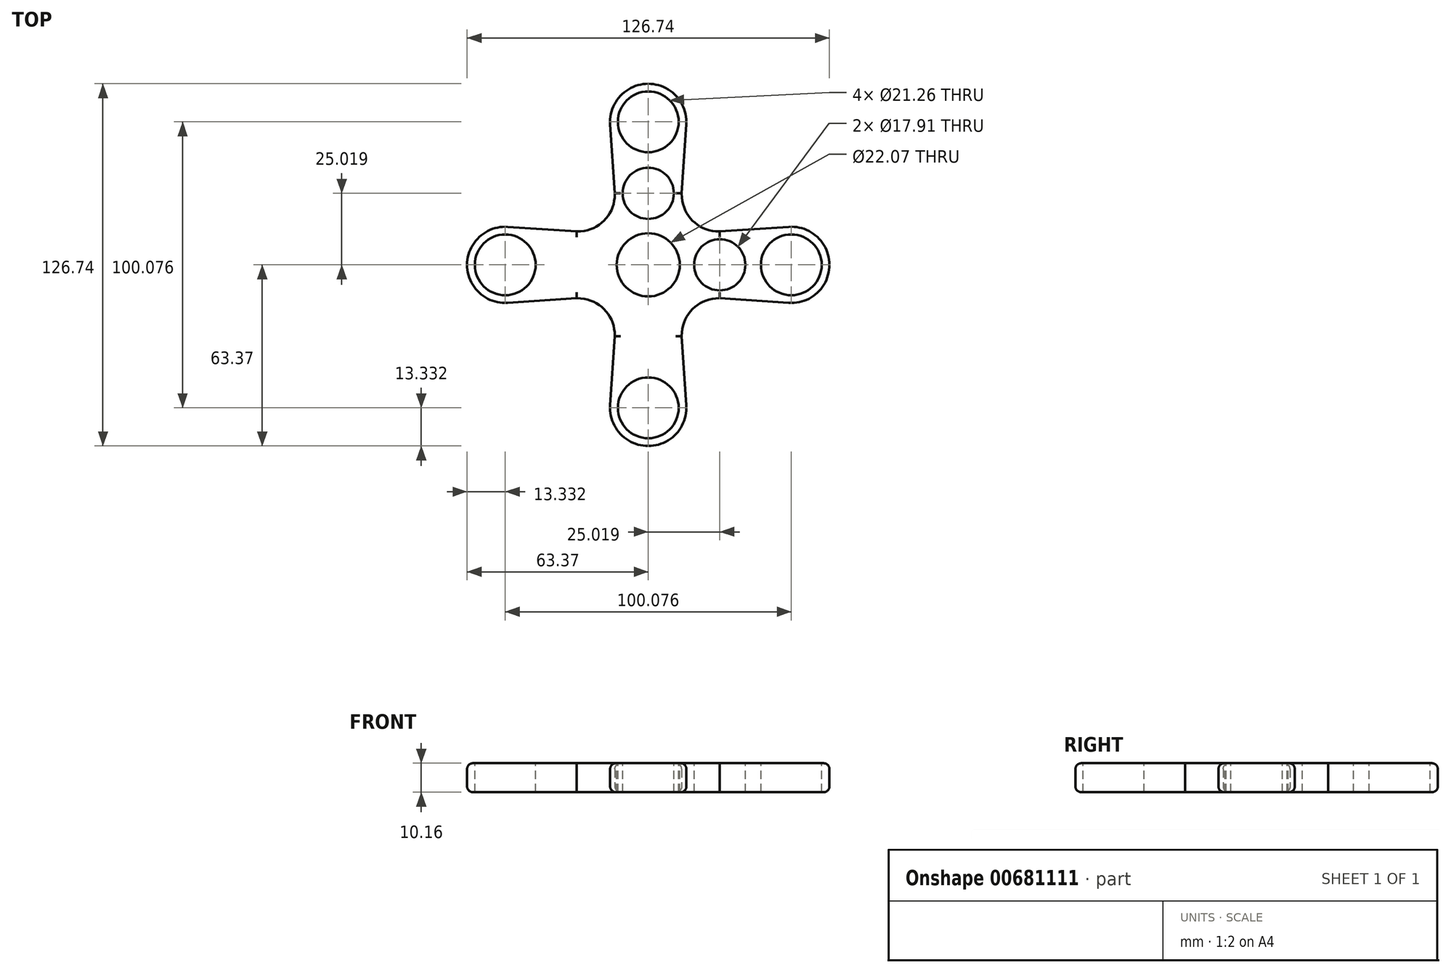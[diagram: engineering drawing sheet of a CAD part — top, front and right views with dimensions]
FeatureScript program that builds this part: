
annotation { "Feature Type Name" : "Feature", "Feature Type Description" : "" }
export const myFeature = defineFeature(function(context is Context, id is Id, definition is map)
    precondition{}
    {
        {
            var Q0;
            Q0=qCreatedBy(makeId("Top.planeOp"),FACE);
            var sketch = newSketch(context, id + "F0", { "sketchPlane" : qUnion([Q0])});
            skCircle(sketch, "E0", {"center": v(0, 0) * mm, "radius": 13.34 * mm});
            skLineSegment(sketch, "E1", {"start": v(0, 0) * mm, "end": v(0, 50.04) * mm});
            skLineSegment(sketch, "E2", {"start": v(0, 0) * mm, "end": v(-50.04, 0) * mm});
            skLineSegment(sketch, "E3", {"start": v(0, 0) * mm, "end": v(50.04, 0) * mm});
            skLineSegment(sketch, "E4", {"start": v(0, 0) * mm, "end": v(0, -50.04) * mm});
            skCircle(sketch, "E5", {"center": v(0, 25.02) * mm, "radius": 11.66 * mm});
            skCircle(sketch, "E6", {"center": v(-25.02, 0) * mm, "radius": 11.66 * mm});
            skCircle(sketch, "E7", {"center": v(25.02, 0) * mm, "radius": 11.66 * mm});
            skCircle(sketch, "E8", {"center": v(0, -25.02) * mm, "radius": 11.66 * mm});
            skCircle(sketch, "E9", {"center": v(0, 50.04) * mm, "radius": 13.34 * mm});
            skCircle(sketch, "E10", {"center": v(-50.04, 0) * mm, "radius": 13.34 * mm});
            skCircle(sketch, "E11", {"center": v(50.04, 0) * mm, "radius": 13.34 * mm});
            skCircle(sketch, "E12", {"center": v(0, -50.04) * mm, "radius": 13.34 * mm});
            skLineSegment(sketch, "E13", {"start": v(-49.14, -13.3) * mm, "end": v(-24.24, -11.63) * mm});
            skLineSegment(sketch, "E14", {"start": v(-49.14, 13.3) * mm, "end": v(-24.24, 11.63) * mm});
            skLineSegment(sketch, "E15", {"start": v(-11.63, -24.24) * mm, "end": v(-13.3, -49.14) * mm});
            skLineSegment(sketch, "E16", {"start": v(11.63, -24.24) * mm, "end": v(13.3, -49.14) * mm});
            skLineSegment(sketch, "E17", {"start": v(24.24, 11.63) * mm, "end": v(49.14, 13.3) * mm});
            skLineSegment(sketch, "E18", {"start": v(24.24, -11.63) * mm, "end": v(49.14, -13.3) * mm});
            skLineSegment(sketch, "E19", {"start": v(-13.3, 49.14) * mm, "end": v(-11.63, 24.24) * mm});
            skLineSegment(sketch, "E20", {"start": v(11.63, 24.24) * mm, "end": v(13.3, 49.14) * mm});
            skLineSegment(sketch, "E21", {"start": v(-25.02, -11.68) * mm, "end": v(-0.9, -13.3) * mm});
            skLineSegment(sketch, "E22", {"start": v(-25.02, 11.68) * mm, "end": v(-0.9, 13.3) * mm});
            skLineSegment(sketch, "E23", {"start": v(-11.68, -25.02) * mm, "end": v(-13.3, -0.9) * mm});
            skLineSegment(sketch, "E24", {"start": v(11.68, -25.02) * mm, "end": v(13.3, -0.9) * mm});
            skLineSegment(sketch, "E25", {"start": v(25.02, -11.68) * mm, "end": v(0.9, -13.3) * mm});
            skLineSegment(sketch, "E26", {"start": v(25.02, 11.68) * mm, "end": v(0.9, 13.3) * mm});
            skLineSegment(sketch, "E27", {"start": v(11.68, 25.02) * mm, "end": v(13.3, 0.9) * mm});
            skLineSegment(sketch, "E28", {"start": v(-11.68, 25.02) * mm, "end": v(-13.3, 0.9) * mm});
            skSolve(sketch);
        }
        {
            var Q0;
            {var subQ0=sQuery(id+"F0.wireOp",EDGE,"E9");var subQ1=makeQuery(id+"F0.imprint","INTERSECT",VERTEX,{"derivedFrom":[subQ0,sQuery(id+"F0.wireOp",EDGE,"E19")]});Q0=makeQuery(id+"F0.imprint","IMPRINT",FACE,{"disambiguationData":[TD([[makeQuery(id+"F0.imprint","IMPRINT",EDGE,{"disambiguationData":[TD([[subQ1,-1.0]])],"derivedFrom":subQ0}),1.0]])]});}
            var Q1;
            {var subQ5=sQuery(id+"F0.wireOp",EDGE,"E9");var subQ7=sQuery(id+"F0.wireOp",EDGE,"E1");var subQ8=makeQuery(id+"F0.imprint","INTERSECT",VERTEX,{"derivedFrom":[subQ7,subQ5]});Q1=makeQuery(id+"F0.imprint","IMPRINT",FACE,{"disambiguationData":[TD([[makeQuery(id+"F0.imprint","IMPRINT",EDGE,{"disambiguationData":[TD([[subQ8,1.0]])],"derivedFrom":subQ7}),1.0]])]});}
            var Q2;
            {var subQ5=sQuery(id+"F0.wireOp",EDGE,"E9");var subQ7=sQuery(id+"F0.wireOp",EDGE,"E1");var subQ8=makeQuery(id+"F0.imprint","INTERSECT",VERTEX,{"derivedFrom":[subQ7,subQ5]});Q2=makeQuery(id+"F0.imprint","IMPRINT",FACE,{"disambiguationData":[TD([[makeQuery(id+"F0.imprint","IMPRINT",EDGE,{"disambiguationData":[TD([[subQ8,1.0]])],"derivedFrom":subQ7}),-1.0]])]});}
            var Q3;
            {var subQ0=sQuery(id+"F0.wireOp",EDGE,"E5");var subQ1=sQuery(id+"F0.wireOp",EDGE,"E1");var subQ2=makeQuery(id+"F0.imprint","INTERSECT",VERTEX,{"disambiguationData":[OD(0.0)],"derivedFrom":[subQ1,subQ0]});Q3=makeQuery(id+"F0.imprint","IMPRINT",FACE,{"disambiguationData":[TD([[makeQuery(id+"F0.imprint","IMPRINT",EDGE,{"disambiguationData":[TD([[subQ2,-1.0]])],"derivedFrom":subQ1}),-1.0]])]});}
            var Q4;
            {var subQ0=sQuery(id+"F0.wireOp",EDGE,"E5");var subQ1=sQuery(id+"F0.wireOp",EDGE,"E1");var subQ2=makeQuery(id+"F0.imprint","INTERSECT",VERTEX,{"disambiguationData":[OD(0.0)],"derivedFrom":[subQ1,subQ0]});Q4=makeQuery(id+"F0.imprint","IMPRINT",FACE,{"disambiguationData":[TD([[makeQuery(id+"F0.imprint","IMPRINT",EDGE,{"disambiguationData":[TD([[subQ2,-1.0]])],"derivedFrom":subQ1}),1.0]])]});}
            var Q5;
            {var subQ0=sQuery(id+"F0.wireOp",EDGE,"E10");var subQ1=makeQuery(id+"F0.imprint","INTERSECT",VERTEX,{"derivedFrom":[subQ0,sQuery(id+"F0.wireOp",EDGE,"E14")]});Q5=makeQuery(id+"F0.imprint","IMPRINT",FACE,{"disambiguationData":[TD([[makeQuery(id+"F0.imprint","IMPRINT",EDGE,{"disambiguationData":[TD([[subQ1,1.0]])],"derivedFrom":subQ0}),1.0]])]});}
            var Q6;
            {var subQ1=sQuery(id+"F0.wireOp",EDGE,"E10");var subQ3=sQuery(id+"F0.wireOp",EDGE,"E2");var subQ4=makeQuery(id+"F0.imprint","INTERSECT",VERTEX,{"derivedFrom":[subQ3,subQ1]});Q6=makeQuery(id+"F0.imprint","IMPRINT",FACE,{"disambiguationData":[TD([[makeQuery(id+"F0.imprint","IMPRINT",EDGE,{"disambiguationData":[TD([[subQ4,1.0]])],"derivedFrom":subQ3}),-1.0]])]});}
            var Q7;
            {var subQ1=sQuery(id+"F0.wireOp",EDGE,"E10");var subQ3=sQuery(id+"F0.wireOp",EDGE,"E2");var subQ4=makeQuery(id+"F0.imprint","INTERSECT",VERTEX,{"derivedFrom":[subQ3,subQ1]});Q7=makeQuery(id+"F0.imprint","IMPRINT",FACE,{"disambiguationData":[TD([[makeQuery(id+"F0.imprint","IMPRINT",EDGE,{"disambiguationData":[TD([[subQ4,1.0]])],"derivedFrom":subQ3}),1.0]])]});}
            var Q8;
            {var subQ0=sQuery(id+"F0.wireOp",EDGE,"E6");var subQ1=sQuery(id+"F0.wireOp",EDGE,"E2");var subQ2=makeQuery(id+"F0.imprint","INTERSECT",VERTEX,{"disambiguationData":[OD(0.0)],"derivedFrom":[subQ1,subQ0]});Q8=makeQuery(id+"F0.imprint","IMPRINT",FACE,{"disambiguationData":[TD([[makeQuery(id+"F0.imprint","IMPRINT",EDGE,{"disambiguationData":[TD([[subQ2,-1.0]])],"derivedFrom":subQ1}),-1.0]])]});}
            var Q9;
            {var subQ0=sQuery(id+"F0.wireOp",EDGE,"E6");var subQ1=sQuery(id+"F0.wireOp",EDGE,"E2");var subQ2=makeQuery(id+"F0.imprint","INTERSECT",VERTEX,{"disambiguationData":[OD(0.0)],"derivedFrom":[subQ1,subQ0]});Q9=makeQuery(id+"F0.imprint","IMPRINT",FACE,{"disambiguationData":[TD([[makeQuery(id+"F0.imprint","IMPRINT",EDGE,{"disambiguationData":[TD([[subQ2,-1.0]])],"derivedFrom":subQ1}),1.0]])]});}
            var Q10;
            {var subQ0=sQuery(id+"F0.wireOp",EDGE,"E12");var subQ1=makeQuery(id+"F0.imprint","INTERSECT",VERTEX,{"derivedFrom":[subQ0,sQuery(id+"F0.wireOp",EDGE,"E16")]});Q10=makeQuery(id+"F0.imprint","IMPRINT",FACE,{"disambiguationData":[TD([[makeQuery(id+"F0.imprint","IMPRINT",EDGE,{"disambiguationData":[TD([[subQ1,-1.0]])],"derivedFrom":subQ0}),1.0]])]});}
            var Q11;
            {var subQ5=sQuery(id+"F0.wireOp",EDGE,"E12");var subQ7=sQuery(id+"F0.wireOp",EDGE,"E4");var subQ8=makeQuery(id+"F0.imprint","INTERSECT",VERTEX,{"derivedFrom":[subQ7,subQ5]});Q11=makeQuery(id+"F0.imprint","IMPRINT",FACE,{"disambiguationData":[TD([[makeQuery(id+"F0.imprint","IMPRINT",EDGE,{"disambiguationData":[TD([[subQ8,1.0]])],"derivedFrom":subQ7}),1.0]])]});}
            var Q12;
            {var subQ5=sQuery(id+"F0.wireOp",EDGE,"E4");var subQ7=sQuery(id+"F0.wireOp",EDGE,"E12");var subQ8=makeQuery(id+"F0.imprint","INTERSECT",VERTEX,{"derivedFrom":[subQ5,subQ7]});Q12=makeQuery(id+"F0.imprint","IMPRINT",FACE,{"disambiguationData":[TD([[makeQuery(id+"F0.imprint","IMPRINT",EDGE,{"disambiguationData":[TD([[subQ8,1.0]])],"derivedFrom":subQ5}),-1.0]])]});}
            var Q13;
            {var subQ0=sQuery(id+"F0.wireOp",EDGE,"E8");var subQ1=sQuery(id+"F0.wireOp",EDGE,"E4");var subQ2=makeQuery(id+"F0.imprint","INTERSECT",VERTEX,{"disambiguationData":[OD(0.0)],"derivedFrom":[subQ1,subQ0]});Q13=makeQuery(id+"F0.imprint","IMPRINT",FACE,{"disambiguationData":[TD([[makeQuery(id+"F0.imprint","IMPRINT",EDGE,{"disambiguationData":[TD([[subQ2,-1.0]])],"derivedFrom":subQ1}),-1.0]])]});}
            var Q14;
            {var subQ0=sQuery(id+"F0.wireOp",EDGE,"E8");var subQ1=sQuery(id+"F0.wireOp",EDGE,"E4");var subQ2=makeQuery(id+"F0.imprint","INTERSECT",VERTEX,{"disambiguationData":[OD(0.0)],"derivedFrom":[subQ1,subQ0]});Q14=makeQuery(id+"F0.imprint","IMPRINT",FACE,{"disambiguationData":[TD([[makeQuery(id+"F0.imprint","IMPRINT",EDGE,{"disambiguationData":[TD([[subQ2,-1.0]])],"derivedFrom":subQ1}),1.0]])]});}
            var Q15;
            {var subQ0=sQuery(id+"F0.wireOp",EDGE,"E7");var subQ1=sQuery(id+"F0.wireOp",EDGE,"E3");var subQ2=makeQuery(id+"F0.imprint","INTERSECT",VERTEX,{"disambiguationData":[OD(0.0)],"derivedFrom":[subQ1,subQ0]});Q15=makeQuery(id+"F0.imprint","IMPRINT",FACE,{"disambiguationData":[TD([[makeQuery(id+"F0.imprint","IMPRINT",EDGE,{"disambiguationData":[TD([[subQ2,-1.0]])],"derivedFrom":subQ1}),-1.0]])]});}
            var Q16;
            {var subQ0=sQuery(id+"F0.wireOp",EDGE,"E7");var subQ1=sQuery(id+"F0.wireOp",EDGE,"E3");var subQ2=makeQuery(id+"F0.imprint","INTERSECT",VERTEX,{"disambiguationData":[OD(0.0)],"derivedFrom":[subQ1,subQ0]});Q16=makeQuery(id+"F0.imprint","IMPRINT",FACE,{"disambiguationData":[TD([[makeQuery(id+"F0.imprint","IMPRINT",EDGE,{"disambiguationData":[TD([[subQ2,-1.0]])],"derivedFrom":subQ1}),1.0]])]});}
            var Q17;
            {var subQ5=sQuery(id+"F0.wireOp",EDGE,"E11");var subQ6=sQuery(id+"F0.wireOp",EDGE,"E3");var subQ7=makeQuery(id+"F0.imprint","INTERSECT",VERTEX,{"derivedFrom":[subQ6,subQ5]});Q17=makeQuery(id+"F0.imprint","IMPRINT",FACE,{"disambiguationData":[TD([[makeQuery(id+"F0.imprint","IMPRINT",EDGE,{"disambiguationData":[TD([[subQ7,1.0]])],"derivedFrom":subQ6}),1.0]])]});}
            var Q18;
            {var subQ5=sQuery(id+"F0.wireOp",EDGE,"E11");var subQ7=sQuery(id+"F0.wireOp",EDGE,"E3");var subQ8=makeQuery(id+"F0.imprint","INTERSECT",VERTEX,{"derivedFrom":[subQ7,subQ5]});Q18=makeQuery(id+"F0.imprint","IMPRINT",FACE,{"disambiguationData":[TD([[makeQuery(id+"F0.imprint","IMPRINT",EDGE,{"disambiguationData":[TD([[subQ8,1.0]])],"derivedFrom":subQ7}),-1.0]])]});}
            var Q19;
            {var subQ0=sQuery(id+"F0.wireOp",EDGE,"E11");var subQ1=makeQuery(id+"F0.imprint","INTERSECT",VERTEX,{"derivedFrom":[subQ0,sQuery(id+"F0.wireOp",EDGE,"E17")]});Q19=makeQuery(id+"F0.imprint","IMPRINT",FACE,{"disambiguationData":[TD([[makeQuery(id+"F0.imprint","IMPRINT",EDGE,{"disambiguationData":[TD([[subQ1,-1.0]])],"derivedFrom":subQ0}),1.0]])]});}
            var Q20;
            {var subQ0=sQuery(id+"F0.wireOp",EDGE,"E0");var subQ6=makeQuery(id+"F0.imprint","INTERSECT",VERTEX,{"derivedFrom":[subQ0,sQuery(id+"F0.wireOp",EDGE,"OeqATU7r-TeiP-DVcz-Oj9g-SgelYqET2oCf")]});Q20=makeQuery(id+"F0.imprint","IMPRINT",FACE,{"disambiguationData":[TD([[makeQuery(id+"F0.imprint","IMPRINT",EDGE,{"disambiguationData":[TD([[subQ6,1.0]])],"derivedFrom":subQ0}),1.0]])]});}
            var Q21;
            {var subQ3=sQuery(id+"F0.wireOp",EDGE,"E0");var subQ6=makeQuery(id+"F0.imprint","INTERSECT",VERTEX,{"derivedFrom":[subQ3,sQuery(id+"F0.wireOp",EDGE,"P4mx4NLA-dkh0-m4Ix-icL6-COEjfOKkm9sa")]});Q21=makeQuery(id+"F0.imprint","IMPRINT",FACE,{"disambiguationData":[TD([[makeQuery(id+"F0.imprint","IMPRINT",EDGE,{"disambiguationData":[TD([[subQ6,1.0]])],"derivedFrom":subQ3}),1.0]])]});}
            var Q22;
            {var subQ3=sQuery(id+"F0.wireOp",EDGE,"E0");var subQ7=makeQuery(id+"F0.imprint","INTERSECT",VERTEX,{"derivedFrom":[subQ3,sQuery(id+"F0.wireOp",EDGE,"11MBrxAj-xtIt-JD5e-sfVu-Mb8FnMuhDSvx")]});Q22=makeQuery(id+"F0.imprint","IMPRINT",FACE,{"disambiguationData":[TD([[makeQuery(id+"F0.imprint","IMPRINT",EDGE,{"disambiguationData":[TD([[subQ7,1.0]])],"derivedFrom":subQ3}),1.0]])]});}
            var Q23;
            {var subQ0=sQuery(id+"F0.wireOp",EDGE,"E0");var subQ4=makeQuery(id+"F0.imprint","INTERSECT",VERTEX,{"derivedFrom":[subQ0,sQuery(id+"F0.wireOp",EDGE,"6knshsRv-X30w-t9dV-kw8X-9zXHXomt9KH4")]});Q23=makeQuery(id+"F0.imprint","IMPRINT",FACE,{"disambiguationData":[TD([[makeQuery(id+"F0.imprint","IMPRINT",EDGE,{"disambiguationData":[TD([[subQ4,1.0]])],"derivedFrom":subQ0}),1.0]])]});}
            var Q24;
            {var subQ0=sQuery(id+"F0.wireOp",EDGE,"6knshsRv-X30w-t9dV-kw8X-9zXHXomt9KH4");var subQ1=sQuery(id+"F0.wireOp",EDGE,"E0");var subQ2=makeQuery(id+"F0.imprint","INTERSECT",VERTEX,{"derivedFrom":[subQ1,subQ0]});Q24=makeQuery(id+"F0.imprint","IMPRINT",FACE,{"disambiguationData":[TD([[makeQuery(id+"F0.imprint","IMPRINT",EDGE,{"disambiguationData":[TD([[subQ2,-1.0]])],"derivedFrom":subQ1}),-1.0]])]});}
            var Q25;
            {var subQ0=sQuery(id+"F0.wireOp",EDGE,"xMuVBNXP-0rYr-ahyC-m8RB-kHPSgdyuj2Vt");var subQ1=sQuery(id+"F0.wireOp",EDGE,"E0");var subQ2=makeQuery(id+"F0.imprint","INTERSECT",VERTEX,{"derivedFrom":[subQ1,subQ0]});Q25=makeQuery(id+"F0.imprint","IMPRINT",FACE,{"disambiguationData":[TD([[makeQuery(id+"F0.imprint","IMPRINT",EDGE,{"disambiguationData":[TD([[subQ2,1.0]])],"derivedFrom":subQ1}),-1.0]])]});}
            var Q26;
            {var subQ0=sQuery(id+"F0.wireOp",EDGE,"11MBrxAj-xtIt-JD5e-sfVu-Mb8FnMuhDSvx");var subQ1=sQuery(id+"F0.wireOp",EDGE,"E0");var subQ2=makeQuery(id+"F0.imprint","INTERSECT",VERTEX,{"derivedFrom":[subQ1,subQ0]});Q26=makeQuery(id+"F0.imprint","IMPRINT",FACE,{"disambiguationData":[TD([[makeQuery(id+"F0.imprint","IMPRINT",EDGE,{"disambiguationData":[TD([[subQ2,-1.0]])],"derivedFrom":subQ1}),-1.0]])]});}
            var Q27;
            {var subQ0=sQuery(id+"F0.wireOp",EDGE,"dGcYwOTv-s8BC-CkCZ-X2qb-BfbS53vJcPqF");var subQ1=sQuery(id+"F0.wireOp",EDGE,"E0");var subQ2=makeQuery(id+"F0.imprint","INTERSECT",VERTEX,{"derivedFrom":[subQ1,subQ0]});Q27=makeQuery(id+"F0.imprint","IMPRINT",FACE,{"disambiguationData":[TD([[makeQuery(id+"F0.imprint","IMPRINT",EDGE,{"disambiguationData":[TD([[subQ2,1.0]])],"derivedFrom":subQ1}),-1.0]])]});}
            var Q28;
            {var subQ5=sQuery(id+"F0.wireOp",EDGE,"E0");var subQ9=sQuery(id+"F0.wireOp",EDGE,"0KCwkMXI-Bwza-oeRS-AiLC-Ybub9KsOqaBf");var subQ11=makeQuery(id+"F0.imprint","INTERSECT",VERTEX,{"derivedFrom":[subQ5,subQ9]});Q28=makeQuery(id+"F0.imprint","IMPRINT",FACE,{"disambiguationData":[TD([[makeQuery(id+"F0.imprint","IMPRINT",EDGE,{"disambiguationData":[TD([[subQ11,-1.0]])],"derivedFrom":subQ5}),-1.0]])]});}
            var Q29;
            {var subQ5=sQuery(id+"F0.wireOp",EDGE,"6knshsRv-X30w-t9dV-kw8X-9zXHXomt9KH4");var subQ9=sQuery(id+"F0.wireOp",EDGE,"E0");var subQ11=makeQuery(id+"F0.imprint","INTERSECT",VERTEX,{"derivedFrom":[subQ9,subQ5]});Q29=makeQuery(id+"F0.imprint","IMPRINT",FACE,{"disambiguationData":[TD([[makeQuery(id+"F0.imprint","IMPRINT",EDGE,{"disambiguationData":[TD([[subQ11,1.0]])],"derivedFrom":subQ9}),-1.0]])]});}
            var Q30;
            {var subQ7=sQuery(id+"F0.wireOp",EDGE,"E28");var subQ8=sQuery(id+"F0.wireOp",EDGE,"E0");var subQ9=makeQuery(id+"F0.imprint","INTERSECT",VERTEX,{"derivedFrom":[subQ8,subQ7]});Q30=makeQuery(id+"F0.imprint","IMPRINT",FACE,{"disambiguationData":[TD([[makeQuery(id+"F0.imprint","IMPRINT",EDGE,{"disambiguationData":[TD([[subQ9,-1.0]])],"derivedFrom":subQ8}),-1.0]])]});}
            var Q31;
            {var subQ7=sQuery(id+"F0.wireOp",EDGE,"E0");var subQ9=sQuery(id+"F0.wireOp",EDGE,"E23");var subQ10=makeQuery(id+"F0.imprint","INTERSECT",VERTEX,{"derivedFrom":[subQ7,subQ9]});Q31=makeQuery(id+"F0.imprint","IMPRINT",FACE,{"disambiguationData":[TD([[makeQuery(id+"F0.imprint","IMPRINT",EDGE,{"disambiguationData":[TD([[subQ10,1.0]])],"derivedFrom":subQ7}),-1.0]])]});}
            var Q32;
            {var subQ5=sQuery(id+"F0.wireOp",EDGE,"E22");var subQ6=sQuery(id+"F0.wireOp",EDGE,"E0");var subQ7=makeQuery(id+"F0.imprint","INTERSECT",VERTEX,{"derivedFrom":[subQ6,subQ5]});Q32=makeQuery(id+"F0.imprint","IMPRINT",FACE,{"disambiguationData":[TD([[makeQuery(id+"F0.imprint","IMPRINT",EDGE,{"disambiguationData":[TD([[subQ7,1.0]])],"derivedFrom":subQ6}),-1.0]])]});}
            var Q33;
            {var subQ7=sQuery(id+"F0.wireOp",EDGE,"E0");var subQ9=sQuery(id+"F0.wireOp",EDGE,"E26");var subQ10=makeQuery(id+"F0.imprint","INTERSECT",VERTEX,{"derivedFrom":[subQ7,subQ9]});Q33=makeQuery(id+"F0.imprint","IMPRINT",FACE,{"disambiguationData":[TD([[makeQuery(id+"F0.imprint","IMPRINT",EDGE,{"disambiguationData":[TD([[subQ10,-1.0]])],"derivedFrom":subQ7}),-1.0]])]});}
            var Q34;
            {var subQ7=sQuery(id+"F0.wireOp",EDGE,"E0");var subQ9=sQuery(id+"F0.wireOp",EDGE,"E27");var subQ10=makeQuery(id+"F0.imprint","INTERSECT",VERTEX,{"derivedFrom":[subQ7,subQ9]});Q34=makeQuery(id+"F0.imprint","IMPRINT",FACE,{"disambiguationData":[TD([[makeQuery(id+"F0.imprint","IMPRINT",EDGE,{"disambiguationData":[TD([[subQ10,1.0]])],"derivedFrom":subQ7}),-1.0]])]});}
            var Q35;
            {var subQ7=sQuery(id+"F0.wireOp",EDGE,"E24");var subQ8=sQuery(id+"F0.wireOp",EDGE,"E0");var subQ9=makeQuery(id+"F0.imprint","INTERSECT",VERTEX,{"derivedFrom":[subQ8,subQ7]});Q35=makeQuery(id+"F0.imprint","IMPRINT",FACE,{"disambiguationData":[TD([[makeQuery(id+"F0.imprint","IMPRINT",EDGE,{"disambiguationData":[TD([[subQ9,-1.0]])],"derivedFrom":subQ8}),-1.0]])]});}
            var Q36;
            {var subQ7=sQuery(id+"F0.wireOp",EDGE,"E0");var subQ9=sQuery(id+"F0.wireOp",EDGE,"E25");var subQ10=makeQuery(id+"F0.imprint","INTERSECT",VERTEX,{"derivedFrom":[subQ7,subQ9]});Q36=makeQuery(id+"F0.imprint","IMPRINT",FACE,{"disambiguationData":[TD([[makeQuery(id+"F0.imprint","IMPRINT",EDGE,{"disambiguationData":[TD([[subQ10,1.0]])],"derivedFrom":subQ7}),-1.0]])]});}
            var Q37;
            {var subQ5=sQuery(id+"F0.wireOp",EDGE,"E21");var subQ6=sQuery(id+"F0.wireOp",EDGE,"E0");var subQ7=makeQuery(id+"F0.imprint","INTERSECT",VERTEX,{"derivedFrom":[subQ6,subQ5]});Q37=makeQuery(id+"F0.imprint","IMPRINT",FACE,{"disambiguationData":[TD([[makeQuery(id+"F0.imprint","IMPRINT",EDGE,{"disambiguationData":[TD([[subQ7,-1.0]])],"derivedFrom":subQ6}),-1.0]])]});}
            extrude(context, id + "F1", {"entities" : qUnion([Q0, Q1, Q2, Q3, Q4, Q5, Q6, Q7, Q8, Q9, Q10, Q11, Q12, Q13, Q14, Q15, Q16, Q17, Q18, Q19, Q20, Q21, Q22, Q23, Q24, Q25, Q26, Q27, Q28, Q29, Q30, Q31, Q32, Q33, Q34, Q35, Q36, Q37]), "depth" : 10.16 * mm, "offsetDistance" : 25.4 * mm});
        }
        {
            var Q0;
            Q0=makeQuery(id+"F1.opExtrude","CAP_FACE",FACE,{"disambiguationData":[OSD([sQuery(id+"F0.wireOp",EDGE,"E9"),sQuery(id+"F0.wireOp",EDGE,"E10"),sQuery(id+"F0.wireOp",EDGE,"E11"),sQuery(id+"F0.wireOp",EDGE,"E12"),sQuery(id+"F0.wireOp",EDGE,"E13"),sQuery(id+"F0.wireOp",EDGE,"E14"),sQuery(id+"F0.wireOp",EDGE,"E15"),sQuery(id+"F0.wireOp",EDGE,"E16"),sQuery(id+"F0.wireOp",EDGE,"E17"),sQuery(id+"F0.wireOp",EDGE,"E18"),sQuery(id+"F0.wireOp",EDGE,"E19"),sQuery(id+"F0.wireOp",EDGE,"E20"),sQuery(id+"F0.wireOp",EDGE,"E21"),sQuery(id+"F0.wireOp",EDGE,"E22"),sQuery(id+"F0.wireOp",EDGE,"E23"),sQuery(id+"F0.wireOp",EDGE,"E24"),sQuery(id+"F0.wireOp",EDGE,"E25"),sQuery(id+"F0.wireOp",EDGE,"E26"),sQuery(id+"F0.wireOp",EDGE,"E27"),sQuery(id+"F0.wireOp",EDGE,"E28")])],"isStart":false});
            var sketch = newSketch(context, id + "F2", { "sketchPlane" : qUnion([Q0])});
            skCircle(sketch, "E29", {"center": v(0, 50.04) * mm, "radius": 10.63 * mm});
            skCircle(sketch, "E30", {"center": v(-50.04, 0) * mm, "radius": 10.63 * mm});
            skCircle(sketch, "E31", {"center": v(50.04, 0) * mm, "radius": 10.63 * mm});
            skCircle(sketch, "E32", {"center": v(0, -50.04) * mm, "radius": 10.63 * mm});
            skCircle(sketch, "E33", {"center": v(0, 0) * mm, "radius": 11.04 * mm});
            skLineSegment(sketch, "E34", {"start": v(0, 0) * mm, "end": v(-50.04, 0) * mm});
            skLineSegment(sketch, "E35", {"start": v(0, 0) * mm, "end": v(50.04, 0) * mm});
            skLineSegment(sketch, "E36", {"start": v(0, 0) * mm, "end": v(0, 50.04) * mm});
            skLineSegment(sketch, "E37", {"start": v(0, 0) * mm, "end": v(0, -50.04) * mm});
            skCircle(sketch, "E38", {"center": v(-25.02, 0) * mm, "radius": 8.95 * mm});
            skCircle(sketch, "E39", {"center": v(25.02, 0) * mm, "radius": 8.95 * mm});
            skCircle(sketch, "E40", {"center": v(0, 25.02) * mm, "radius": 8.95 * mm});
            skCircle(sketch, "E41", {"center": v(0, -25.02) * mm, "radius": 8.95 * mm});
            skSolve(sketch);
        }
        {
            var Q0;
            Q0=makeQuery(id+"F2.imprint","IMPRINT",FACE,{"disambiguationData":[TD([[makeQuery(id+"F2.imprint","IMPRINT",EDGE,{"derivedFrom":sQuery(id+"F2.wireOp",EDGE,"E29")}),1.0]])]});
            var Q1;
            Q1=makeQuery(id+"F2.imprint","IMPRINT",FACE,{"disambiguationData":[TD([[makeQuery(id+"F2.imprint","IMPRINT",EDGE,{"derivedFrom":sQuery(id+"F2.wireOp",EDGE,"E30")}),1.0]])]});
            var Q2;
            Q2=makeQuery(id+"F2.imprint","IMPRINT",FACE,{"disambiguationData":[TD([[makeQuery(id+"F2.imprint","IMPRINT",EDGE,{"derivedFrom":sQuery(id+"F2.wireOp",EDGE,"E33")}),1.0]])]});
            var Q3;
            Q3=makeQuery(id+"F2.imprint","IMPRINT",FACE,{"disambiguationData":[TD([[makeQuery(id+"F2.imprint","IMPRINT",EDGE,{"derivedFrom":sQuery(id+"F2.wireOp",EDGE,"E31")}),1.0]])]});
            var Q4;
            Q4=makeQuery(id+"F2.imprint","IMPRINT",FACE,{"disambiguationData":[TD([[makeQuery(id+"F2.imprint","IMPRINT",EDGE,{"derivedFrom":sQuery(id+"F2.wireOp",EDGE,"E32")}),1.0]])]});
            var Q5;
            {var subQ0=sQuery(id+"F2.wireOp",EDGE,"P7v9rNYd-zsm6-EBDp-hEL1-8AicFUI8aBt1");var subQ1=sQuery(id+"F2.wireOp",EDGE,"E34");var subQ2=makeQuery(id+"F2.imprint","INTERSECT",VERTEX,{"disambiguationData":[OD(0.0)],"derivedFrom":[subQ1,subQ0]});Q5=makeQuery(id+"F2.imprint","IMPRINT",FACE,{"disambiguationData":[TD([[makeQuery(id+"F2.imprint","IMPRINT",EDGE,{"disambiguationData":[TD([[subQ2,1.0]])],"derivedFrom":subQ1}),-1.0]])]});}
            var Q6;
            {var subQ0=sQuery(id+"F2.wireOp",EDGE,"P7v9rNYd-zsm6-EBDp-hEL1-8AicFUI8aBt1");var subQ1=sQuery(id+"F2.wireOp",EDGE,"E34");var subQ2=makeQuery(id+"F2.imprint","INTERSECT",VERTEX,{"disambiguationData":[OD(0.0)],"derivedFrom":[subQ1,subQ0]});Q6=makeQuery(id+"F2.imprint","IMPRINT",FACE,{"disambiguationData":[TD([[makeQuery(id+"F2.imprint","IMPRINT",EDGE,{"disambiguationData":[TD([[subQ2,1.0]])],"derivedFrom":subQ1}),1.0]])]});}
            var Q7;
            {var subQ0=sQuery(id+"F2.wireOp",EDGE,"sgpK4NKR-6yXJ-TN63-0nZW-uHVtksImcnuz");var subQ1=sQuery(id+"F2.wireOp",EDGE,"E36");var subQ2=makeQuery(id+"F2.imprint","INTERSECT",VERTEX,{"disambiguationData":[OD(0.0)],"derivedFrom":[subQ1,subQ0]});Q7=makeQuery(id+"F2.imprint","IMPRINT",FACE,{"disambiguationData":[TD([[makeQuery(id+"F2.imprint","IMPRINT",EDGE,{"disambiguationData":[TD([[subQ2,-1.0]])],"derivedFrom":subQ1}),1.0]])]});}
            var Q8;
            {var subQ0=sQuery(id+"F2.wireOp",EDGE,"sgpK4NKR-6yXJ-TN63-0nZW-uHVtksImcnuz");var subQ1=sQuery(id+"F2.wireOp",EDGE,"E36");var subQ2=makeQuery(id+"F2.imprint","INTERSECT",VERTEX,{"disambiguationData":[OD(0.0)],"derivedFrom":[subQ1,subQ0]});Q8=makeQuery(id+"F2.imprint","IMPRINT",FACE,{"disambiguationData":[TD([[makeQuery(id+"F2.imprint","IMPRINT",EDGE,{"disambiguationData":[TD([[subQ2,-1.0]])],"derivedFrom":subQ1}),-1.0]])]});}
            var Q9;
            {var subQ0=sQuery(id+"F2.wireOp",EDGE,"QqMhnWJU-l4oD-vyuv-57R4-FaOAJUmgMaoE");var subQ1=sQuery(id+"F2.wireOp",EDGE,"E35");var subQ2=makeQuery(id+"F2.imprint","INTERSECT",VERTEX,{"disambiguationData":[OD(0.0)],"derivedFrom":[subQ1,subQ0]});Q9=makeQuery(id+"F2.imprint","IMPRINT",FACE,{"disambiguationData":[TD([[makeQuery(id+"F2.imprint","IMPRINT",EDGE,{"disambiguationData":[TD([[subQ2,-1.0]])],"derivedFrom":subQ1}),1.0]])]});}
            var Q10;
            {var subQ0=sQuery(id+"F2.wireOp",EDGE,"QqMhnWJU-l4oD-vyuv-57R4-FaOAJUmgMaoE");var subQ1=sQuery(id+"F2.wireOp",EDGE,"E35");var subQ2=makeQuery(id+"F2.imprint","INTERSECT",VERTEX,{"disambiguationData":[OD(0.0)],"derivedFrom":[subQ1,subQ0]});Q10=makeQuery(id+"F2.imprint","IMPRINT",FACE,{"disambiguationData":[TD([[makeQuery(id+"F2.imprint","IMPRINT",EDGE,{"disambiguationData":[TD([[subQ2,-1.0]])],"derivedFrom":subQ1}),-1.0]])]});}
            var Q11;
            {var subQ0=sQuery(id+"F2.wireOp",EDGE,"5nZpbu1R-FvPb-eCDr-ticD-0d8ufeMjPlMW");var subQ1=sQuery(id+"F2.wireOp",EDGE,"E37");var subQ2=makeQuery(id+"F2.imprint","INTERSECT",VERTEX,{"disambiguationData":[OD(0.0)],"derivedFrom":[subQ1,subQ0]});Q11=makeQuery(id+"F2.imprint","IMPRINT",FACE,{"disambiguationData":[TD([[makeQuery(id+"F2.imprint","IMPRINT",EDGE,{"disambiguationData":[TD([[subQ2,1.0]])],"derivedFrom":subQ1}),-1.0]])]});}
            var Q12;
            {var subQ0=sQuery(id+"F2.wireOp",EDGE,"5nZpbu1R-FvPb-eCDr-ticD-0d8ufeMjPlMW");var subQ1=sQuery(id+"F2.wireOp",EDGE,"E37");var subQ2=makeQuery(id+"F2.imprint","INTERSECT",VERTEX,{"disambiguationData":[OD(0.0)],"derivedFrom":[subQ1,subQ0]});Q12=makeQuery(id+"F2.imprint","IMPRINT",FACE,{"disambiguationData":[TD([[makeQuery(id+"F2.imprint","IMPRINT",EDGE,{"disambiguationData":[TD([[subQ2,1.0]])],"derivedFrom":subQ1}),1.0]])]});}
            var Q13;
            {var subQ0=sQuery(id+"F2.wireOp",EDGE,"E38");var subQ1=sQuery(id+"F2.wireOp",EDGE,"E34");var subQ2=makeQuery(id+"F2.imprint","INTERSECT",VERTEX,{"disambiguationData":[OD(0.0)],"derivedFrom":[subQ1,subQ0]});Q13=makeQuery(id+"F2.imprint","IMPRINT",FACE,{"disambiguationData":[TD([[makeQuery(id+"F2.imprint","IMPRINT",EDGE,{"disambiguationData":[TD([[subQ2,1.0]])],"derivedFrom":subQ1}),-1.0]])]});}
            var Q14;
            {var subQ0=sQuery(id+"F2.wireOp",EDGE,"E38");var subQ1=sQuery(id+"F2.wireOp",EDGE,"E34");var subQ2=makeQuery(id+"F2.imprint","INTERSECT",VERTEX,{"disambiguationData":[OD(0.0)],"derivedFrom":[subQ1,subQ0]});Q14=makeQuery(id+"F2.imprint","IMPRINT",FACE,{"disambiguationData":[TD([[makeQuery(id+"F2.imprint","IMPRINT",EDGE,{"disambiguationData":[TD([[subQ2,1.0]])],"derivedFrom":subQ1}),1.0]])]});}
            var Q15;
            {var subQ0=sQuery(id+"F2.wireOp",EDGE,"E40");var subQ1=sQuery(id+"F2.wireOp",EDGE,"E36");var subQ2=makeQuery(id+"F2.imprint","INTERSECT",VERTEX,{"disambiguationData":[OD(0.0)],"derivedFrom":[subQ1,subQ0]});Q15=makeQuery(id+"F2.imprint","IMPRINT",FACE,{"disambiguationData":[TD([[makeQuery(id+"F2.imprint","IMPRINT",EDGE,{"disambiguationData":[TD([[subQ2,-1.0]])],"derivedFrom":subQ1}),1.0]])]});}
            var Q16;
            {var subQ0=sQuery(id+"F2.wireOp",EDGE,"E40");var subQ1=sQuery(id+"F2.wireOp",EDGE,"E36");var subQ2=makeQuery(id+"F2.imprint","INTERSECT",VERTEX,{"disambiguationData":[OD(0.0)],"derivedFrom":[subQ1,subQ0]});Q16=makeQuery(id+"F2.imprint","IMPRINT",FACE,{"disambiguationData":[TD([[makeQuery(id+"F2.imprint","IMPRINT",EDGE,{"disambiguationData":[TD([[subQ2,-1.0]])],"derivedFrom":subQ1}),-1.0]])]});}
            var Q17;
            {var subQ0=sQuery(id+"F2.wireOp",EDGE,"E39");var subQ1=sQuery(id+"F2.wireOp",EDGE,"E35");var subQ2=makeQuery(id+"F2.imprint","INTERSECT",VERTEX,{"disambiguationData":[OD(0.0)],"derivedFrom":[subQ1,subQ0]});Q17=makeQuery(id+"F2.imprint","IMPRINT",FACE,{"disambiguationData":[TD([[makeQuery(id+"F2.imprint","IMPRINT",EDGE,{"disambiguationData":[TD([[subQ2,-1.0]])],"derivedFrom":subQ1}),1.0]])]});}
            var Q18;
            {var subQ0=sQuery(id+"F2.wireOp",EDGE,"E39");var subQ1=sQuery(id+"F2.wireOp",EDGE,"E35");var subQ2=makeQuery(id+"F2.imprint","INTERSECT",VERTEX,{"disambiguationData":[OD(0.0)],"derivedFrom":[subQ1,subQ0]});Q18=makeQuery(id+"F2.imprint","IMPRINT",FACE,{"disambiguationData":[TD([[makeQuery(id+"F2.imprint","IMPRINT",EDGE,{"disambiguationData":[TD([[subQ2,-1.0]])],"derivedFrom":subQ1}),-1.0]])]});}
            var Q19;
            {var subQ0=sQuery(id+"F2.wireOp",EDGE,"E41");var subQ1=sQuery(id+"F2.wireOp",EDGE,"E37");var subQ2=makeQuery(id+"F2.imprint","INTERSECT",VERTEX,{"disambiguationData":[OD(0.0)],"derivedFrom":[subQ1,subQ0]});Q19=makeQuery(id+"F2.imprint","IMPRINT",FACE,{"disambiguationData":[TD([[makeQuery(id+"F2.imprint","IMPRINT",EDGE,{"disambiguationData":[TD([[subQ2,1.0]])],"derivedFrom":subQ1}),1.0]])]});}
            var Q20;
            {var subQ0=sQuery(id+"F2.wireOp",EDGE,"E41");var subQ1=sQuery(id+"F2.wireOp",EDGE,"E37");var subQ2=makeQuery(id+"F2.imprint","INTERSECT",VERTEX,{"disambiguationData":[OD(0.0)],"derivedFrom":[subQ1,subQ0]});Q20=makeQuery(id+"F2.imprint","IMPRINT",FACE,{"disambiguationData":[TD([[makeQuery(id+"F2.imprint","IMPRINT",EDGE,{"disambiguationData":[TD([[subQ2,1.0]])],"derivedFrom":subQ1}),-1.0]])]});}
            var Q21;
            Q21=makeQuery(id+"F1.opExtrude","CAP_FACE",FACE,{"disambiguationData":[OSD([sQuery(id+"F0.wireOp",EDGE,"E9"),sQuery(id+"F0.wireOp",EDGE,"E10"),sQuery(id+"F0.wireOp",EDGE,"E11"),sQuery(id+"F0.wireOp",EDGE,"E12"),sQuery(id+"F0.wireOp",EDGE,"E13"),sQuery(id+"F0.wireOp",EDGE,"E14"),sQuery(id+"F0.wireOp",EDGE,"E15"),sQuery(id+"F0.wireOp",EDGE,"E16"),sQuery(id+"F0.wireOp",EDGE,"E17"),sQuery(id+"F0.wireOp",EDGE,"E18"),sQuery(id+"F0.wireOp",EDGE,"E19"),sQuery(id+"F0.wireOp",EDGE,"E20"),sQuery(id+"F0.wireOp",EDGE,"E21"),sQuery(id+"F0.wireOp",EDGE,"E22"),sQuery(id+"F0.wireOp",EDGE,"E23"),sQuery(id+"F0.wireOp",EDGE,"E24"),sQuery(id+"F0.wireOp",EDGE,"E25"),sQuery(id+"F0.wireOp",EDGE,"E26"),sQuery(id+"F0.wireOp",EDGE,"E27"),sQuery(id+"F0.wireOp",EDGE,"E28")])],"isStart":true});
            extrude(context, id + "F3", {"entities" : qUnion([Q0, Q1, Q2, Q3, Q4, Q5, Q6, Q7, Q8, Q9, Q10, Q11, Q12, Q13, Q14, Q15, Q16, Q17, Q18, Q19, Q20]), "operationType" : NewBodyOperationType.REMOVE, "endBound" : BoundingType.UP_TO_SURFACE, "oppositeDirection" : true, "depth" : 25.4 * mm, "endBoundEntityFace" : qUnion([Q21]), "offsetDistance" : 25.4 * mm});
        }
        {
            var Q0;
            Q0=makeQuery(id+"F1.opExtrude","SWEPT_EDGE",EDGE,{"disambiguationData":[OSD([sQuery(id+"F0.wireOp",EDGE,"E22"),sQuery(id+"F0.wireOp",EDGE,"E28")])]});
            var Q1;
            Q1=makeQuery(id+"F1.opExtrude","SWEPT_EDGE",EDGE,{"disambiguationData":[OSD([sQuery(id+"F0.wireOp",EDGE,"E26"),sQuery(id+"F0.wireOp",EDGE,"E27")])]});
            var Q2;
            Q2=makeQuery(id+"F1.opExtrude","SWEPT_EDGE",EDGE,{"disambiguationData":[OSD([sQuery(id+"F0.wireOp",EDGE,"E24"),sQuery(id+"F0.wireOp",EDGE,"E25")])]});
            var Q3;
            Q3=makeQuery(id+"F1.opExtrude","SWEPT_EDGE",EDGE,{"disambiguationData":[OSD([sQuery(id+"F0.wireOp",EDGE,"E21"),sQuery(id+"F0.wireOp",EDGE,"E23")])]});
            fillet(context, id + "F4", {"entities" : qUnion([Q0, Q1, Q2, Q3]), "radius" : 12.7 * mm, "tangentPropagation" : true, "allowEdgeOverflow" : false});
        }
        {
            var Q0;
            Q0=makeQuery(id+"F1.opExtrude","CAP_EDGE",EDGE,{"disambiguationData":[OSD([sQuery(id+"F0.wireOp",EDGE,"E13")])],"isStart":false});
            var Q1;
            Q1=makeQuery(id+"F1.opExtrude","CAP_EDGE",EDGE,{"disambiguationData":[OSD([sQuery(id+"F0.wireOp",EDGE,"E21")])],"isStart":false});
            var Q2;
            Q2=makeQuery(id+"F1.opExtrude","CAP_EDGE",EDGE,{"disambiguationData":[OSD([sQuery(id+"F0.wireOp",EDGE,"E15")])],"isStart":false});
            var Q3;
            {var subQ0=sQuery(id+"F0.wireOp",EDGE,"E25");var subQ1=sQuery(id+"F0.wireOp",EDGE,"E24");Q3=makeQuery(id+"F4.opFillet","BLEND_EDGE",EDGE,{"blendedFrom":[makeQuery(id+"F1.opExtrude","SWEPT_EDGE",EDGE,{"disambiguationData":[OSD([subQ1,subQ0])]}),makeQuery(id+"F1.opExtrude","CAP_FACE",FACE,{"disambiguationData":[OSD([sQuery(id+"F0.wireOp",EDGE,"E9"),sQuery(id+"F0.wireOp",EDGE,"E10"),sQuery(id+"F0.wireOp",EDGE,"E11"),sQuery(id+"F0.wireOp",EDGE,"E12"),sQuery(id+"F0.wireOp",EDGE,"E13"),sQuery(id+"F0.wireOp",EDGE,"E14"),sQuery(id+"F0.wireOp",EDGE,"E15"),sQuery(id+"F0.wireOp",EDGE,"E16"),sQuery(id+"F0.wireOp",EDGE,"E17"),sQuery(id+"F0.wireOp",EDGE,"E18"),sQuery(id+"F0.wireOp",EDGE,"E19"),sQuery(id+"F0.wireOp",EDGE,"E20"),sQuery(id+"F0.wireOp",EDGE,"E21"),sQuery(id+"F0.wireOp",EDGE,"E22"),sQuery(id+"F0.wireOp",EDGE,"E23"),subQ1,subQ0,sQuery(id+"F0.wireOp",EDGE,"E26"),sQuery(id+"F0.wireOp",EDGE,"E27"),sQuery(id+"F0.wireOp",EDGE,"E28")])],"isStart":false})],"blendedInto":[makeQuery(id+"F1.opExtrude","CAP_FACE",FACE,{"disambiguationData":[OSD([sQuery(id+"F0.wireOp",EDGE,"E9"),sQuery(id+"F0.wireOp",EDGE,"E10"),sQuery(id+"F0.wireOp",EDGE,"E11"),sQuery(id+"F0.wireOp",EDGE,"E12"),sQuery(id+"F0.wireOp",EDGE,"E13"),sQuery(id+"F0.wireOp",EDGE,"E14"),sQuery(id+"F0.wireOp",EDGE,"E15"),sQuery(id+"F0.wireOp",EDGE,"E16"),sQuery(id+"F0.wireOp",EDGE,"E17"),sQuery(id+"F0.wireOp",EDGE,"E18"),sQuery(id+"F0.wireOp",EDGE,"E19"),sQuery(id+"F0.wireOp",EDGE,"E20"),sQuery(id+"F0.wireOp",EDGE,"E21"),sQuery(id+"F0.wireOp",EDGE,"E22"),sQuery(id+"F0.wireOp",EDGE,"E23"),subQ1,subQ0,sQuery(id+"F0.wireOp",EDGE,"E26"),sQuery(id+"F0.wireOp",EDGE,"E27"),sQuery(id+"F0.wireOp",EDGE,"E28")])],"isStart":false})]});}
            var Q4;
            Q4=makeQuery(id+"F1.opExtrude","CAP_EDGE",EDGE,{"disambiguationData":[OSD([sQuery(id+"F0.wireOp",EDGE,"E18")])],"isStart":false});
            var Q5;
            {var subQ0=sQuery(id+"F0.wireOp",EDGE,"E27");var subQ1=sQuery(id+"F0.wireOp",EDGE,"E26");Q5=makeQuery(id+"F4.opFillet","BLEND_EDGE",EDGE,{"blendedFrom":[makeQuery(id+"F1.opExtrude","SWEPT_EDGE",EDGE,{"disambiguationData":[OSD([subQ1,subQ0])]}),makeQuery(id+"F1.opExtrude","CAP_FACE",FACE,{"disambiguationData":[OSD([sQuery(id+"F0.wireOp",EDGE,"E9"),sQuery(id+"F0.wireOp",EDGE,"E10"),sQuery(id+"F0.wireOp",EDGE,"E11"),sQuery(id+"F0.wireOp",EDGE,"E12"),sQuery(id+"F0.wireOp",EDGE,"E13"),sQuery(id+"F0.wireOp",EDGE,"E14"),sQuery(id+"F0.wireOp",EDGE,"E15"),sQuery(id+"F0.wireOp",EDGE,"E16"),sQuery(id+"F0.wireOp",EDGE,"E17"),sQuery(id+"F0.wireOp",EDGE,"E18"),sQuery(id+"F0.wireOp",EDGE,"E19"),sQuery(id+"F0.wireOp",EDGE,"E20"),sQuery(id+"F0.wireOp",EDGE,"E21"),sQuery(id+"F0.wireOp",EDGE,"E22"),sQuery(id+"F0.wireOp",EDGE,"E23"),sQuery(id+"F0.wireOp",EDGE,"E24"),sQuery(id+"F0.wireOp",EDGE,"E25"),subQ1,subQ0,sQuery(id+"F0.wireOp",EDGE,"E28")])],"isStart":false})],"blendedInto":[makeQuery(id+"F1.opExtrude","CAP_FACE",FACE,{"disambiguationData":[OSD([sQuery(id+"F0.wireOp",EDGE,"E9"),sQuery(id+"F0.wireOp",EDGE,"E10"),sQuery(id+"F0.wireOp",EDGE,"E11"),sQuery(id+"F0.wireOp",EDGE,"E12"),sQuery(id+"F0.wireOp",EDGE,"E13"),sQuery(id+"F0.wireOp",EDGE,"E14"),sQuery(id+"F0.wireOp",EDGE,"E15"),sQuery(id+"F0.wireOp",EDGE,"E16"),sQuery(id+"F0.wireOp",EDGE,"E17"),sQuery(id+"F0.wireOp",EDGE,"E18"),sQuery(id+"F0.wireOp",EDGE,"E19"),sQuery(id+"F0.wireOp",EDGE,"E20"),sQuery(id+"F0.wireOp",EDGE,"E21"),sQuery(id+"F0.wireOp",EDGE,"E22"),sQuery(id+"F0.wireOp",EDGE,"E23"),sQuery(id+"F0.wireOp",EDGE,"E24"),sQuery(id+"F0.wireOp",EDGE,"E25"),subQ1,subQ0,sQuery(id+"F0.wireOp",EDGE,"E28")])],"isStart":false})]});}
            var Q6;
            Q6=makeQuery(id+"F1.opExtrude","CAP_EDGE",EDGE,{"disambiguationData":[OSD([sQuery(id+"F0.wireOp",EDGE,"E20")])],"isStart":false});
            var Q7;
            {var subQ0=sQuery(id+"F0.wireOp",EDGE,"E28");var subQ1=sQuery(id+"F0.wireOp",EDGE,"E22");Q7=makeQuery(id+"F4.opFillet","BLEND_EDGE",EDGE,{"blendedFrom":[makeQuery(id+"F1.opExtrude","SWEPT_EDGE",EDGE,{"disambiguationData":[OSD([subQ1,subQ0])]}),makeQuery(id+"F1.opExtrude","CAP_FACE",FACE,{"disambiguationData":[OSD([sQuery(id+"F0.wireOp",EDGE,"E9"),sQuery(id+"F0.wireOp",EDGE,"E10"),sQuery(id+"F0.wireOp",EDGE,"E11"),sQuery(id+"F0.wireOp",EDGE,"E12"),sQuery(id+"F0.wireOp",EDGE,"E13"),sQuery(id+"F0.wireOp",EDGE,"E14"),sQuery(id+"F0.wireOp",EDGE,"E15"),sQuery(id+"F0.wireOp",EDGE,"E16"),sQuery(id+"F0.wireOp",EDGE,"E17"),sQuery(id+"F0.wireOp",EDGE,"E18"),sQuery(id+"F0.wireOp",EDGE,"E19"),sQuery(id+"F0.wireOp",EDGE,"E20"),sQuery(id+"F0.wireOp",EDGE,"E21"),subQ1,sQuery(id+"F0.wireOp",EDGE,"E23"),sQuery(id+"F0.wireOp",EDGE,"E24"),sQuery(id+"F0.wireOp",EDGE,"E25"),sQuery(id+"F0.wireOp",EDGE,"E26"),sQuery(id+"F0.wireOp",EDGE,"E27"),subQ0])],"isStart":false})],"blendedInto":[makeQuery(id+"F1.opExtrude","CAP_FACE",FACE,{"disambiguationData":[OSD([sQuery(id+"F0.wireOp",EDGE,"E9"),sQuery(id+"F0.wireOp",EDGE,"E10"),sQuery(id+"F0.wireOp",EDGE,"E11"),sQuery(id+"F0.wireOp",EDGE,"E12"),sQuery(id+"F0.wireOp",EDGE,"E13"),sQuery(id+"F0.wireOp",EDGE,"E14"),sQuery(id+"F0.wireOp",EDGE,"E15"),sQuery(id+"F0.wireOp",EDGE,"E16"),sQuery(id+"F0.wireOp",EDGE,"E17"),sQuery(id+"F0.wireOp",EDGE,"E18"),sQuery(id+"F0.wireOp",EDGE,"E19"),sQuery(id+"F0.wireOp",EDGE,"E20"),sQuery(id+"F0.wireOp",EDGE,"E21"),subQ1,sQuery(id+"F0.wireOp",EDGE,"E23"),sQuery(id+"F0.wireOp",EDGE,"E24"),sQuery(id+"F0.wireOp",EDGE,"E25"),sQuery(id+"F0.wireOp",EDGE,"E26"),sQuery(id+"F0.wireOp",EDGE,"E27"),subQ0])],"isStart":false})]});}
            var Q8;
            Q8=makeQuery(id+"F1.opExtrude","CAP_EDGE",EDGE,{"disambiguationData":[OSD([sQuery(id+"F0.wireOp",EDGE,"E16")])],"isStart":true});
            var Q9;
            {var subQ0=sQuery(id+"F0.wireOp",EDGE,"E25");var subQ1=sQuery(id+"F0.wireOp",EDGE,"E24");Q9=makeQuery(id+"F4.opFillet","BLEND_EDGE",EDGE,{"blendedFrom":[makeQuery(id+"F1.opExtrude","SWEPT_EDGE",EDGE,{"disambiguationData":[OSD([subQ1,subQ0])]}),makeQuery(id+"F1.opExtrude","CAP_FACE",FACE,{"disambiguationData":[OSD([sQuery(id+"F0.wireOp",EDGE,"E9"),sQuery(id+"F0.wireOp",EDGE,"E10"),sQuery(id+"F0.wireOp",EDGE,"E11"),sQuery(id+"F0.wireOp",EDGE,"E12"),sQuery(id+"F0.wireOp",EDGE,"E13"),sQuery(id+"F0.wireOp",EDGE,"E14"),sQuery(id+"F0.wireOp",EDGE,"E15"),sQuery(id+"F0.wireOp",EDGE,"E16"),sQuery(id+"F0.wireOp",EDGE,"E17"),sQuery(id+"F0.wireOp",EDGE,"E18"),sQuery(id+"F0.wireOp",EDGE,"E19"),sQuery(id+"F0.wireOp",EDGE,"E20"),sQuery(id+"F0.wireOp",EDGE,"E21"),sQuery(id+"F0.wireOp",EDGE,"E22"),sQuery(id+"F0.wireOp",EDGE,"E23"),subQ1,subQ0,sQuery(id+"F0.wireOp",EDGE,"E26"),sQuery(id+"F0.wireOp",EDGE,"E27"),sQuery(id+"F0.wireOp",EDGE,"E28")])],"isStart":true})],"blendedInto":[makeQuery(id+"F1.opExtrude","CAP_FACE",FACE,{"disambiguationData":[OSD([sQuery(id+"F0.wireOp",EDGE,"E9"),sQuery(id+"F0.wireOp",EDGE,"E10"),sQuery(id+"F0.wireOp",EDGE,"E11"),sQuery(id+"F0.wireOp",EDGE,"E12"),sQuery(id+"F0.wireOp",EDGE,"E13"),sQuery(id+"F0.wireOp",EDGE,"E14"),sQuery(id+"F0.wireOp",EDGE,"E15"),sQuery(id+"F0.wireOp",EDGE,"E16"),sQuery(id+"F0.wireOp",EDGE,"E17"),sQuery(id+"F0.wireOp",EDGE,"E18"),sQuery(id+"F0.wireOp",EDGE,"E19"),sQuery(id+"F0.wireOp",EDGE,"E20"),sQuery(id+"F0.wireOp",EDGE,"E21"),sQuery(id+"F0.wireOp",EDGE,"E22"),sQuery(id+"F0.wireOp",EDGE,"E23"),subQ1,subQ0,sQuery(id+"F0.wireOp",EDGE,"E26"),sQuery(id+"F0.wireOp",EDGE,"E27"),sQuery(id+"F0.wireOp",EDGE,"E28")])],"isStart":true})]});}
            var Q10;
            Q10=makeQuery(id+"F1.opExtrude","CAP_EDGE",EDGE,{"disambiguationData":[OSD([sQuery(id+"F0.wireOp",EDGE,"E18")])],"isStart":true});
            var Q11;
            Q11=makeQuery(id+"F1.opExtrude","CAP_EDGE",EDGE,{"disambiguationData":[OSD([sQuery(id+"F0.wireOp",EDGE,"E20")])],"isStart":true});
            var Q12;
            {var subQ0=sQuery(id+"F0.wireOp",EDGE,"E27");var subQ1=sQuery(id+"F0.wireOp",EDGE,"E26");Q12=makeQuery(id+"F4.opFillet","BLEND_EDGE",EDGE,{"blendedFrom":[makeQuery(id+"F1.opExtrude","SWEPT_EDGE",EDGE,{"disambiguationData":[OSD([subQ1,subQ0])]}),makeQuery(id+"F1.opExtrude","CAP_FACE",FACE,{"disambiguationData":[OSD([sQuery(id+"F0.wireOp",EDGE,"E9"),sQuery(id+"F0.wireOp",EDGE,"E10"),sQuery(id+"F0.wireOp",EDGE,"E11"),sQuery(id+"F0.wireOp",EDGE,"E12"),sQuery(id+"F0.wireOp",EDGE,"E13"),sQuery(id+"F0.wireOp",EDGE,"E14"),sQuery(id+"F0.wireOp",EDGE,"E15"),sQuery(id+"F0.wireOp",EDGE,"E16"),sQuery(id+"F0.wireOp",EDGE,"E17"),sQuery(id+"F0.wireOp",EDGE,"E18"),sQuery(id+"F0.wireOp",EDGE,"E19"),sQuery(id+"F0.wireOp",EDGE,"E20"),sQuery(id+"F0.wireOp",EDGE,"E21"),sQuery(id+"F0.wireOp",EDGE,"E22"),sQuery(id+"F0.wireOp",EDGE,"E23"),sQuery(id+"F0.wireOp",EDGE,"E24"),sQuery(id+"F0.wireOp",EDGE,"E25"),subQ1,subQ0,sQuery(id+"F0.wireOp",EDGE,"E28")])],"isStart":true})],"blendedInto":[makeQuery(id+"F1.opExtrude","CAP_FACE",FACE,{"disambiguationData":[OSD([sQuery(id+"F0.wireOp",EDGE,"E9"),sQuery(id+"F0.wireOp",EDGE,"E10"),sQuery(id+"F0.wireOp",EDGE,"E11"),sQuery(id+"F0.wireOp",EDGE,"E12"),sQuery(id+"F0.wireOp",EDGE,"E13"),sQuery(id+"F0.wireOp",EDGE,"E14"),sQuery(id+"F0.wireOp",EDGE,"E15"),sQuery(id+"F0.wireOp",EDGE,"E16"),sQuery(id+"F0.wireOp",EDGE,"E17"),sQuery(id+"F0.wireOp",EDGE,"E18"),sQuery(id+"F0.wireOp",EDGE,"E19"),sQuery(id+"F0.wireOp",EDGE,"E20"),sQuery(id+"F0.wireOp",EDGE,"E21"),sQuery(id+"F0.wireOp",EDGE,"E22"),sQuery(id+"F0.wireOp",EDGE,"E23"),sQuery(id+"F0.wireOp",EDGE,"E24"),sQuery(id+"F0.wireOp",EDGE,"E25"),subQ1,subQ0,sQuery(id+"F0.wireOp",EDGE,"E28")])],"isStart":true})]});}
            var Q13;
            {var subQ0=sQuery(id+"F0.wireOp",EDGE,"E28");var subQ1=sQuery(id+"F0.wireOp",EDGE,"E22");Q13=makeQuery(id+"F4.opFillet","BLEND_EDGE",EDGE,{"blendedFrom":[makeQuery(id+"F1.opExtrude","SWEPT_EDGE",EDGE,{"disambiguationData":[OSD([subQ1,subQ0])]}),makeQuery(id+"F1.opExtrude","CAP_FACE",FACE,{"disambiguationData":[OSD([sQuery(id+"F0.wireOp",EDGE,"E9"),sQuery(id+"F0.wireOp",EDGE,"E10"),sQuery(id+"F0.wireOp",EDGE,"E11"),sQuery(id+"F0.wireOp",EDGE,"E12"),sQuery(id+"F0.wireOp",EDGE,"E13"),sQuery(id+"F0.wireOp",EDGE,"E14"),sQuery(id+"F0.wireOp",EDGE,"E15"),sQuery(id+"F0.wireOp",EDGE,"E16"),sQuery(id+"F0.wireOp",EDGE,"E17"),sQuery(id+"F0.wireOp",EDGE,"E18"),sQuery(id+"F0.wireOp",EDGE,"E19"),sQuery(id+"F0.wireOp",EDGE,"E20"),sQuery(id+"F0.wireOp",EDGE,"E21"),subQ1,sQuery(id+"F0.wireOp",EDGE,"E23"),sQuery(id+"F0.wireOp",EDGE,"E24"),sQuery(id+"F0.wireOp",EDGE,"E25"),sQuery(id+"F0.wireOp",EDGE,"E26"),sQuery(id+"F0.wireOp",EDGE,"E27"),subQ0])],"isStart":true})],"blendedInto":[makeQuery(id+"F1.opExtrude","CAP_FACE",FACE,{"disambiguationData":[OSD([sQuery(id+"F0.wireOp",EDGE,"E9"),sQuery(id+"F0.wireOp",EDGE,"E10"),sQuery(id+"F0.wireOp",EDGE,"E11"),sQuery(id+"F0.wireOp",EDGE,"E12"),sQuery(id+"F0.wireOp",EDGE,"E13"),sQuery(id+"F0.wireOp",EDGE,"E14"),sQuery(id+"F0.wireOp",EDGE,"E15"),sQuery(id+"F0.wireOp",EDGE,"E16"),sQuery(id+"F0.wireOp",EDGE,"E17"),sQuery(id+"F0.wireOp",EDGE,"E18"),sQuery(id+"F0.wireOp",EDGE,"E19"),sQuery(id+"F0.wireOp",EDGE,"E20"),sQuery(id+"F0.wireOp",EDGE,"E21"),subQ1,sQuery(id+"F0.wireOp",EDGE,"E23"),sQuery(id+"F0.wireOp",EDGE,"E24"),sQuery(id+"F0.wireOp",EDGE,"E25"),sQuery(id+"F0.wireOp",EDGE,"E26"),sQuery(id+"F0.wireOp",EDGE,"E27"),subQ0])],"isStart":true})]});}
            var Q14;
            Q14=makeQuery(id+"F1.opExtrude","CAP_EDGE",EDGE,{"disambiguationData":[OSD([sQuery(id+"F0.wireOp",EDGE,"E14")])],"isStart":true});
            var Q15;
            Q15=makeQuery(id+"F1.opExtrude","CAP_EDGE",EDGE,{"disambiguationData":[OSD([sQuery(id+"F0.wireOp",EDGE,"E21")])],"isStart":true});
            fillet(context, id + "F5", {"entities" : qUnion([Q0, Q1, Q2, Q3, Q4, Q5, Q6, Q7, Q8, Q9, Q10, Q11, Q12, Q13, Q14, Q15]), "radius" : 2.03 * mm, "tangentPropagation" : true, "allowEdgeOverflow" : false});
        }
    });
